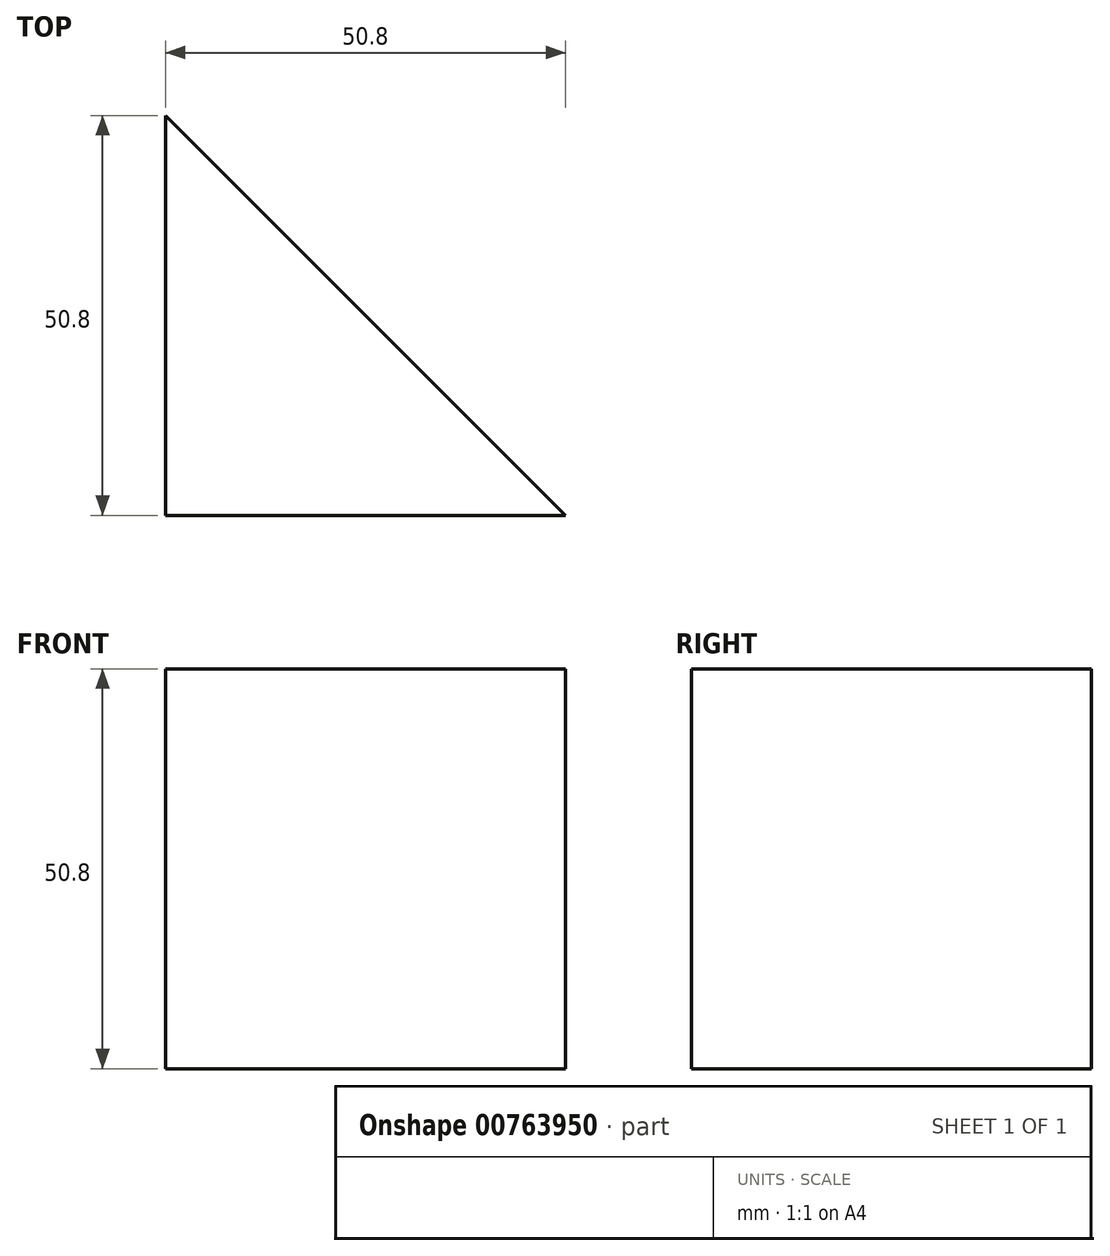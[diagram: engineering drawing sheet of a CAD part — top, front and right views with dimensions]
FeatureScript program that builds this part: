
annotation { "Feature Type Name" : "Feature", "Feature Type Description" : "" }
export const myFeature = defineFeature(function(context is Context, id is Id, definition is map)
    precondition{}
    {
        {
            var Q0;
            Q0=qCreatedBy(makeId("Top.planeOp"),FACE);
            var sketch = newSketch(context, id + "F0", { "sketchPlane" : qUnion([Q0])});
            skLineSegment(sketch, "E0", {"start": v(0, 0) * mm, "end": v(0, 50.8) * mm});
            skLineSegment(sketch, "E1", {"start": v(0, 0) * mm, "end": v(50.8, 0) * mm});
            skLineSegment(sketch, "E2", {"start": v(0, 50.8) * mm, "end": v(50.8, 0) * mm});
            skSolve(sketch);
        }
        {
            var Q0;
            Q0=makeQuery(id+"F0.imprint","IMPRINT",FACE,{"disambiguationData":[TD([[makeQuery(id+"F0.imprint","IMPRINT",EDGE,{"derivedFrom":sQuery(id+"F0.wireOp",EDGE,"E0")}),-1.0]])]});
            extrude(context, id + "F1", {"entities" : qUnion([Q0]), "depth" : 50.8 * mm, "offsetDistance" : 25.4 * mm});
        }
    });
